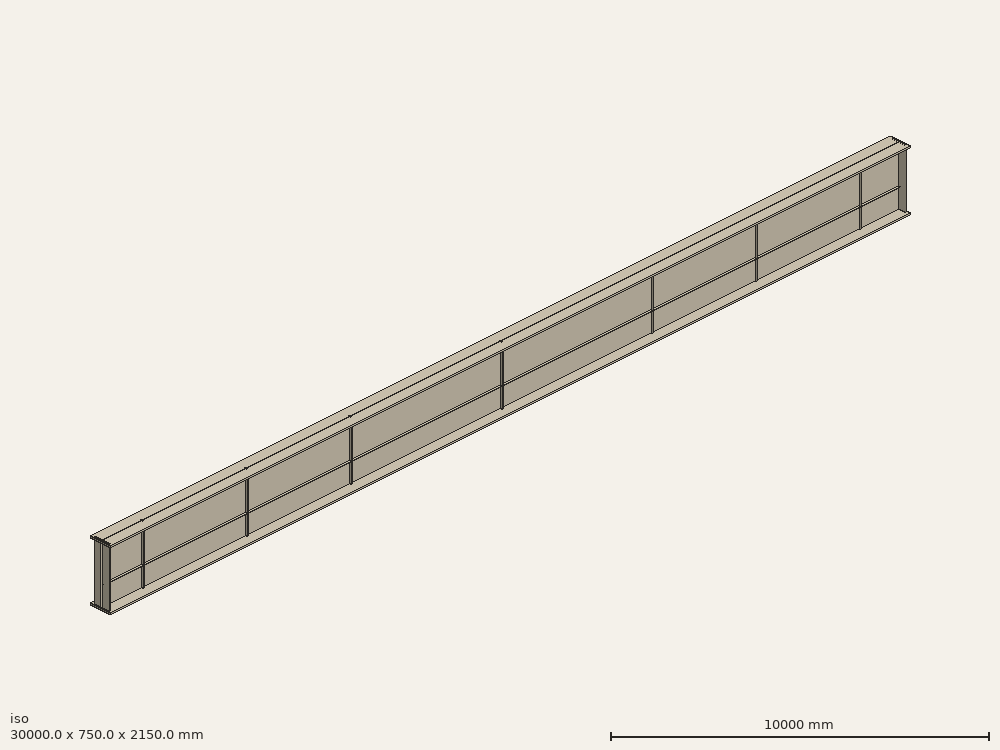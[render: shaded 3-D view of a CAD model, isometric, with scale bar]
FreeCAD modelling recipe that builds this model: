
FCSTD DOCUMENT  (FreeCAD 0.21R33771 (Git))
Label: Plate_girder_EC3_hvl
License: All rights reserved
LicenseURL: http://en.wikipedia.org/wiki/All_rights_reserved
objects: Sketcher::SketchObject×13, Part::Extrusion×13, Fem::ConstraintForce×5, Part::FeaturePython×2, Fem::ConstraintDisplacement×2, Fem::FemSolverObjectPython×1, App::MaterialObjectPython×1, Fem::FemMeshObjectPython×1, Fem::FemAnalysis×1, Part::Part2DObjectPython×1
note: 29 computed .brp shape members not serialized (recipe doc carries the construction recipe); baked Part::Feature solids carry a one-line shape summary decoded from their .brp

FEATURE [Fem::FemSolverObjectPython] SolverCcxTools  # FEM object (typed FeaturePython)
  AnalysisType = 0
  BeamShellResultOutput3D = false
  BucklingFactors = 1
  EigenmodeHighLimit = 1000000
  EigenmodeLowLimit = 0
  EigenmodesCount = 10
  GeometricalNonlinearity = 0
  IterationsControlParameterCutb = 0.25,0.5,0.75,0.85,,,1.5,
  IterationsControlParameterIter = 4,8,9,200,10,400,,200,,
  IterationsControlParameterTimeUse = false
  IterationsThermoMechMaximum = 2000
  IterationsUserDefinedIncrementations = false
  IterationsUserDefinedTimeStepLength = false
  MaterialNonlinearity = 0
  MatrixSolverType = 0
  SplitInputWriter = false
  ThermoMechSteadyState = true
  TimeEnd = 1
  TimeInitialStep = 0.01
FEATURE [App::MaterialObjectPython] MaterialSolid  # material (typed FeaturePython)
  Category = 0
  Material = AuthorAndLicense=(c) 2014 M. Münch - GNU Lesser General Public License (LGPL),CardName=Steel-St-E-315,Density=7800 kg/m^3,Father=Metal,+13 more (map truncated)
FEATURE [Sketcher::SketchObject] Sketch001  label="end stiffener"
  FullyConstrained = true
  Placement = pos=(0,0,0) rot=(0.57735,0.57735,0.57735;2.0944rad)
  sketch-geometry (4):
    g0: LineSegment StartX=87.5 StartY=2100 StartZ=0 EndX=662.5 EndY=2100 EndZ=0
    g1: LineSegment StartX=662.5 StartY=2100 StartZ=0 EndX=662.5 EndY=0 EndZ=0
    g2: LineSegment StartX=662.5 StartY=0 StartZ=0 EndX=87.5 EndY=0 EndZ=0
    g3: LineSegment StartX=87.5 StartY=0 StartZ=0 EndX=87.5 EndY=2100 EndZ=0
  constraints (12):
    c: Coincident(g0,g1)
    c: Coincident(g1,g2)
    c: Coincident(g2,g3)
    c: Coincident(g3,g0)
    c: Horizontal(g0)
    c: Horizontal(g2)
    c: Vertical(g1)
    c: Vertical(g3)
    c: DistanceY(g1,g1) = 2100
    c: PointOnObject(g2,g-1)
    c: DistanceX(g2,g2) = 575
    c: DistanceX(g-1,g2) = 87.5
FEATURE [Sketcher::SketchObject] Sketch002  label="stiffener"
  FullyConstrained = true
  Placement = pos=(0,0,0) rot=(0.57735,0.57735,0.57735;2.0944rad)
  sketch-geometry (4):
    g0: LineSegment StartX=287.5 StartY=2100 StartZ=0 EndX=462.5 EndY=2100 EndZ=0
    g1: LineSegment StartX=462.5 StartY=2100 StartZ=0 EndX=462.5 EndY=0 EndZ=0
    g2: LineSegment StartX=462.5 StartY=0 StartZ=0 EndX=287.5 EndY=0 EndZ=0
    g3: LineSegment StartX=287.5 StartY=0 StartZ=0 EndX=287.5 EndY=2100 EndZ=0
  constraints (12):
    c: Coincident(g0,g1)
    c: Coincident(g1,g2)
    c: Coincident(g2,g3)
    c: Coincident(g3,g0)
    c: Horizontal(g0)
    c: Horizontal(g2)
    c: Vertical(g1)
    c: Vertical(g3)
    c: DistanceY(g1,g1) = 2100
    c: PointOnObject(g2,g-1)
    c: DistanceX(g0,g0) = 175
    c: DistanceX(g-1,g2) = 287.5
FEATURE [Sketcher::SketchObject] Sketch003
  FullyConstrained = true
  sketch-geometry (4):
    g0: LineSegment StartX=0 StartY=462.5 StartZ=0 EndX=175 EndY=462.5 EndZ=0
    g1: LineSegment StartX=175 StartY=462.5 StartZ=0 EndX=175 EndY=287.5 EndZ=0
    g2: LineSegment StartX=175 StartY=287.5 StartZ=0 EndX=0 EndY=287.5 EndZ=0
    g3: LineSegment StartX=0 StartY=287.5 StartZ=0 EndX=0 EndY=462.5 EndZ=0
  constraints (12):
    c: Coincident(g0,g1)
    c: Coincident(g1,g2)
    c: Coincident(g2,g3)
    c: Coincident(g3,g0)
    c: Horizontal(g0)
    c: Horizontal(g2)
    c: Vertical(g1)
    c: Vertical(g3)
    c: DistanceX(g0,g0) = 175
    c: DistanceY(g1,g1) = 175
    c: PointOnObject(g2,g-2)
    c: DistanceY(g-1,g2) = 287.5
FEATURE [Part::Extrusion] Extrude001  label="load pad"
  Base = -> Sketch003
  Dir = (0,0,1)
  DirMode = 2
  FaceMakerClass = Part::FaceMakerBullseye
  LengthFwd = 0
  LengthRev = 50
  Placement = pos=(9262.5,0,0) rot=(0,0,1;0rad)
  Solid = true
  Symmetric = false
FEATURE [Part::Extrusion] Extrude002  label="stiffener001"
  Base = -> Sketch002
  Dir = (1,0,0)
  DirMode = 2
  FaceMakerClass = Part::FaceMakerBullseye
  LengthFwd = 15
  LengthRev = 0
  Placement = pos=(1542.5,0,0) rot=(0,0,1;0rad)
  Solid = true
  Symmetric = false
FEATURE [Part::Extrusion] Extrude003  label="end stiffener001"
  Base = -> Sketch001
  Dir = (1,0,0)
  DirMode = 2
  FaceMakerClass = Part::FaceMakerBullseye
  LengthFwd = 24
  LengthRev = 0
  Placement = pos=(50,0,0) rot=(0,0,1;0rad)
  Solid = true
  Symmetric = false
FEATURE [Sketcher::SketchObject] Sketch004  label="end stiffener003"
  FullyConstrained = true
  Placement = pos=(0,0,0) rot=(0.57735,0.57735,0.57735;2.0944rad)
  sketch-geometry (4):
    g0: LineSegment StartX=87.5 StartY=2100 StartZ=0 EndX=662.5 EndY=2100 EndZ=0
    g1: LineSegment StartX=662.5 StartY=2100 StartZ=0 EndX=662.5 EndY=0 EndZ=0
    g2: LineSegment StartX=662.5 StartY=0 StartZ=0 EndX=87.5 EndY=0 EndZ=0
    g3: LineSegment StartX=87.5 StartY=0 StartZ=0 EndX=87.5 EndY=2100 EndZ=0
  constraints (12):
    c: Coincident(g0,g1)
    c: Coincident(g1,g2)
    c: Coincident(g2,g3)
    c: Coincident(g3,g0)
    c: Horizontal(g0)
    c: Horizontal(g2)
    c: Vertical(g1)
    c: Vertical(g3)
    c: DistanceY(g1,g1) = 2100
    c: PointOnObject(g2,g-1)
    c: DistanceX(g2,g2) = 575
    c: DistanceX(g-1,g2) = 87.5
FEATURE [Part::Extrusion] Extrude004  label="end stiffener002"
  Base = -> Sketch004
  Dir = (1,0,0)
  DirMode = 2
  FaceMakerClass = Part::FaceMakerBullseye
  LengthFwd = 24
  LengthRev = 0
  Placement = pos=(29926,0,0) rot=(0,0,1;0rad)
  Solid = true
  Symmetric = false
FEATURE [Sketcher::SketchObject] Sketch005  label="stiffener003"
  FullyConstrained = true
  Placement = pos=(0,0,0) rot=(0.57735,0.57735,0.57735;2.0944rad)
  sketch-geometry (4):
    g0: LineSegment StartX=287.5 StartY=2100 StartZ=0 EndX=462.5 EndY=2100 EndZ=0
    g1: LineSegment StartX=462.5 StartY=2100 StartZ=0 EndX=462.5 EndY=0 EndZ=0
    g2: LineSegment StartX=462.5 StartY=0 StartZ=0 EndX=287.5 EndY=0 EndZ=0
    g3: LineSegment StartX=287.5 StartY=0 StartZ=0 EndX=287.5 EndY=2100 EndZ=0
  constraints (12):
    c: Coincident(g0,g1)
    c: Coincident(g1,g2)
    c: Coincident(g2,g3)
    c: Coincident(g3,g0)
    c: Horizontal(g0)
    c: Horizontal(g2)
    c: Vertical(g1)
    c: Vertical(g3)
    c: DistanceY(g1,g1) = 2100
    c: PointOnObject(g2,g-1)
    c: DistanceX(g0,g0) = 175
    c: DistanceX(g-1,g2) = 287.5
FEATURE [Part::Extrusion] Extrude005  label="stiffener002"
  Base = -> Sketch005
  Dir = (1,0,0)
  DirMode = 2
  FaceMakerClass = Part::FaceMakerBullseye
  LengthFwd = 15
  LengthRev = 0
  Placement = pos=(5442.5,0,0) rot=(0,0,1;0rad)
  Solid = true
  Symmetric = false
FEATURE [Sketcher::SketchObject] Sketch006  label="stiffener005"
  FullyConstrained = true
  Placement = pos=(0,0,0) rot=(0.57735,0.57735,0.57735;2.0944rad)
  sketch-geometry (4):
    g0: LineSegment StartX=287.5 StartY=2100 StartZ=0 EndX=462.5 EndY=2100 EndZ=0
    g1: LineSegment StartX=462.5 StartY=2100 StartZ=0 EndX=462.5 EndY=0 EndZ=0
    g2: LineSegment StartX=462.5 StartY=0 StartZ=0 EndX=287.5 EndY=0 EndZ=0
    g3: LineSegment StartX=287.5 StartY=0 StartZ=0 EndX=287.5 EndY=2100 EndZ=0
  constraints (12):
    c: Coincident(g0,g1)
    c: Coincident(g1,g2)
    c: Coincident(g2,g3)
    c: Coincident(g3,g0)
    c: Horizontal(g0)
    c: Horizontal(g2)
    c: Vertical(g1)
    c: Vertical(g3)
    c: DistanceY(g1,g1) = 2100
    c: PointOnObject(g2,g-1)
    c: DistanceX(g0,g0) = 175
    c: DistanceX(g-1,g2) = 287.5
FEATURE [Part::Extrusion] Extrude006  label="stiffener004"
  Base = -> Sketch006
  Dir = (1,0,0)
  DirMode = 2
  FaceMakerClass = Part::FaceMakerBullseye
  LengthFwd = 15
  LengthRev = 0
  Placement = pos=(9342.5,0,0) rot=(0,0,1;0rad)
  Solid = true
  Symmetric = false
FEATURE [Sketcher::SketchObject] Sketch007  label="stiffener007"
  FullyConstrained = true
  Placement = pos=(0,0,0) rot=(0.57735,0.57735,0.57735;2.0944rad)
  sketch-geometry (4):
    g0: LineSegment StartX=287.5 StartY=2100 StartZ=0 EndX=462.5 EndY=2100 EndZ=0
    g1: LineSegment StartX=462.5 StartY=2100 StartZ=0 EndX=462.5 EndY=0 EndZ=0
    g2: LineSegment StartX=462.5 StartY=0 StartZ=0 EndX=287.5 EndY=0 EndZ=0
    g3: LineSegment StartX=287.5 StartY=0 StartZ=0 EndX=287.5 EndY=2100 EndZ=0
  constraints (12):
    c: Coincident(g0,g1)
    c: Coincident(g1,g2)
    c: Coincident(g2,g3)
    c: Coincident(g3,g0)
    c: Horizontal(g0)
    c: Horizontal(g2)
    c: Vertical(g1)
    c: Vertical(g3)
    c: DistanceY(g1,g1) = 2100
    c: PointOnObject(g2,g-1)
    c: DistanceX(g0,g0) = 175
    c: DistanceX(g-1,g2) = 287.5
FEATURE [Part::Extrusion] Extrude007  label="stiffener006"
  Base = -> Sketch007
  Dir = (1,0,0)
  DirMode = 2
  FaceMakerClass = Part::FaceMakerBullseye
  LengthFwd = 15
  LengthRev = 0
  Placement = pos=(14992.5,0,0) rot=(0,0,1;0rad)
  Solid = true
  Symmetric = false
FEATURE [Sketcher::SketchObject] Sketch008  label="stiffener009"
  FullyConstrained = true
  Placement = pos=(0,0,0) rot=(0.57735,0.57735,0.57735;2.0944rad)
  sketch-geometry (4):
    g0: LineSegment StartX=287.5 StartY=2100 StartZ=0 EndX=462.5 EndY=2100 EndZ=0
    g1: LineSegment StartX=462.5 StartY=2100 StartZ=0 EndX=462.5 EndY=0 EndZ=0
    g2: LineSegment StartX=462.5 StartY=0 StartZ=0 EndX=287.5 EndY=0 EndZ=0
    g3: LineSegment StartX=287.5 StartY=0 StartZ=0 EndX=287.5 EndY=2100 EndZ=0
  constraints (12):
    c: Coincident(g0,g1)
    c: Coincident(g1,g2)
    c: Coincident(g2,g3)
    c: Coincident(g3,g0)
    c: Horizontal(g0)
    c: Horizontal(g2)
    c: Vertical(g1)
    c: Vertical(g3)
    c: DistanceY(g1,g1) = 2100
    c: PointOnObject(g2,g-1)
    c: DistanceX(g0,g0) = 175
    c: DistanceX(g-1,g2) = 287.5
FEATURE [Part::Extrusion] Extrude008  label="stiffener008"
  Base = -> Sketch008
  Dir = (1,0,0)
  DirMode = 2
  FaceMakerClass = Part::FaceMakerBullseye
  LengthFwd = 15
  LengthRev = 0
  Placement = pos=(20642.5,0,0) rot=(0,0,1;0rad)
  Solid = true
  Symmetric = false
FEATURE [Sketcher::SketchObject] Sketch009  label="stiffener011"
  FullyConstrained = true
  Placement = pos=(0,0,0) rot=(0.57735,0.57735,0.57735;2.0944rad)
  sketch-geometry (4):
    g0: LineSegment StartX=287.5 StartY=2100 StartZ=0 EndX=462.5 EndY=2100 EndZ=0
    g1: LineSegment StartX=462.5 StartY=2100 StartZ=0 EndX=462.5 EndY=0 EndZ=0
    g2: LineSegment StartX=462.5 StartY=0 StartZ=0 EndX=287.5 EndY=0 EndZ=0
    g3: LineSegment StartX=287.5 StartY=0 StartZ=0 EndX=287.5 EndY=2100 EndZ=0
  constraints (12):
    c: Coincident(g0,g1)
    c: Coincident(g1,g2)
    c: Coincident(g2,g3)
    c: Coincident(g3,g0)
    c: Horizontal(g0)
    c: Horizontal(g2)
    c: Vertical(g1)
    c: Vertical(g3)
    c: DistanceY(g1,g1) = 2100
    c: PointOnObject(g2,g-1)
    c: DistanceX(g0,g0) = 175
    c: DistanceX(g-1,g2) = 287.5
FEATURE [Part::Extrusion] Extrude009  label="stiffener010"
  Base = -> Sketch009
  Dir = (1,0,0)
  DirMode = 2
  FaceMakerClass = Part::FaceMakerBullseye
  LengthFwd = 15
  LengthRev = 0
  Placement = pos=(24542.5,0,0) rot=(0,0,1;0rad)
  Solid = true
  Symmetric = false
FEATURE [Sketcher::SketchObject] Sketch010  label="stiffener013"
  FullyConstrained = true
  Placement = pos=(0,0,0) rot=(0.57735,0.57735,0.57735;2.0944rad)
  sketch-geometry (4):
    g0: LineSegment StartX=287.5 StartY=2100 StartZ=0 EndX=462.5 EndY=2100 EndZ=0
    g1: LineSegment StartX=462.5 StartY=2100 StartZ=0 EndX=462.5 EndY=0 EndZ=0
    g2: LineSegment StartX=462.5 StartY=0 StartZ=0 EndX=287.5 EndY=0 EndZ=0
    g3: LineSegment StartX=287.5 StartY=0 StartZ=0 EndX=287.5 EndY=2100 EndZ=0
  constraints (12):
    c: Coincident(g0,g1)
    c: Coincident(g1,g2)
    c: Coincident(g2,g3)
    c: Coincident(g3,g0)
    c: Horizontal(g0)
    c: Horizontal(g2)
    c: Vertical(g1)
    c: Vertical(g3)
    c: DistanceY(g1,g1) = 2100
    c: PointOnObject(g2,g-1)
    c: DistanceX(g0,g0) = 175
    c: DistanceX(g-1,g2) = 287.5
FEATURE [Part::Extrusion] Extrude010  label="stiffener012"
  Base = -> Sketch010
  Dir = (1,0,0)
  DirMode = 2
  FaceMakerClass = Part::FaceMakerBullseye
  LengthFwd = 15
  LengthRev = 0
  Placement = pos=(28442.5,0,0) rot=(0,0,1;0rad)
  Solid = true
  Symmetric = false
FEATURE [Sketcher::SketchObject] Sketch  label="girder"
  FullyConstrained = true
  Placement = pos=(0,0,0) rot=(0.57735,0.57735,0.57735;2.0944rad)
  sketch-geometry (16):
    g0: LineSegment StartX=750 StartY=2100 StartZ=0 EndX=750 EndY=2050 EndZ=0
    g1: LineSegment StartX=750 StartY=2050 StartZ=0 EndX=382.5 EndY=2050 EndZ=0
    g2: LineSegment StartX=382.5 StartY=2050 StartZ=0 EndX=382.5 EndY=50 EndZ=0
    g3: LineSegment StartX=382.5 StartY=50 StartZ=0 EndX=750 EndY=50 EndZ=0
    g4: LineSegment StartX=750 StartY=50 StartZ=0 EndX=750 EndY=0 EndZ=0
    g5: LineSegment StartX=0 StartY=0 StartZ=0 EndX=0 EndY=50 EndZ=0
    g6: LineSegment StartX=0 StartY=50 StartZ=0 EndX=367.5 EndY=50 EndZ=0
    g7: LineSegment StartX=367.5 StartY=50 StartZ=0 EndX=367.5 EndY=2050 EndZ=0
    g8: LineSegment StartX=367.5 StartY=2050 StartZ=0 EndX=0 EndY=2050 EndZ=0
    g9: LineSegment StartX=750 StartY=2100 StartZ=0 EndX=382.5 EndY=2100 EndZ=0
    g10: LineSegment StartX=750 StartY=0 StartZ=0 EndX=382.5 EndY=0 EndZ=0
    g11: LineSegment StartX=367.5 StartY=0 StartZ=0 EndX=0 EndY=0 EndZ=0
    g12: LineSegment StartX=382.5 StartY=2100 StartZ=0 EndX=367.5 EndY=2100 EndZ=0
    g13: LineSegment StartX=0 StartY=2050 StartZ=0 EndX=0 EndY=2100 EndZ=0
    g14: LineSegment StartX=367.5 StartY=0 StartZ=0 EndX=382.5 EndY=0 EndZ=0
    g15: LineSegment StartX=0 StartY=2100 StartZ=0 EndX=367.5 EndY=2100 EndZ=0
  constraints (48):
    c: Vertical(g0)
    c: Coincident(g0,g1)
    c: Horizontal(g1)
    c: Coincident(g1,g2)
    c: Vertical(g2)
    c: Coincident(g2,g3)
    c: Horizontal(g3)
    c: Coincident(g3,g4)
    c: PointOnObject(g4,g-1)
    c: Vertical(g5)
    c: Coincident(g5,g6)
    c: Horizontal(g6)
    c: Coincident(g6,g7)
    c: Vertical(g7)
    c: Coincident(g7,g8)
    c: Horizontal(g8)
    c: Vertical(g4)
    c: DistanceY(g0,g0) = 50
    c: DistanceX(g6,g6) = 367.5
    c: DistanceX(g3,g3) = 367.5
    c: DistanceY(g4,g4) = 50
    c: DistanceY(g5,g5) = 50
    c: DistanceY(g4,g0) = 2100
    c: DistanceX(g-1,g5) = 0
    c: Coincident(g9,g0)
    c: Horizontal(g9)
    c: Coincident(g10,g4)
    c: Horizontal(g10)
    c: Coincident(g11,g5)
    c: Horizontal(g11)
    c: Coincident(g12,g9)
    c: Horizontal(g12)
    c: Coincident(g13,g8)
    c: Vertical(g13)
    c: DistanceX(g7,g1) = 15
    c: Equal(g11,g6)
    c: Equal(g10,g3)
    c: Coincident(g14,g11)
    c: Coincident(g14,g10)
    c: DistanceY(g13,g13) = 50
    c: DistanceY(g-1,g5) = 0
    c: Coincident(g15,g13)
    c: Coincident(g15,g12)
    c: Horizontal(g15)
    c: DistanceX(g15,g15) = 367.5
    c: DistanceX(g12,g12) = 15
    c: DistanceX(g9,g9) = 367.5
    c: PointOnObject(g13,g-2)
FEATURE [Part::Extrusion] Extrude
  Base = -> Sketch
  Dir = (1,0,0)
  DirMode = 2
  FaceMakerClass = Part::FaceMakerBullseye
  LengthFwd = 30000
  LengthRev = 0
  Solid = true
  Symmetric = false
FEATURE [Sketcher::SketchObject] Sketch011
  FullyConstrained = true
  sketch-geometry (4):
    g0: LineSegment StartX=0 StartY=462.5 StartZ=0 EndX=175 EndY=462.5 EndZ=0
    g1: LineSegment StartX=175 StartY=462.5 StartZ=0 EndX=175 EndY=287.5 EndZ=0
    g2: LineSegment StartX=175 StartY=287.5 StartZ=0 EndX=0 EndY=287.5 EndZ=0
    g3: LineSegment StartX=0 StartY=287.5 StartZ=0 EndX=0 EndY=462.5 EndZ=0
  constraints (12):
    c: Coincident(g0,g1)
    c: Coincident(g1,g2)
    c: Coincident(g2,g3)
    c: Coincident(g3,g0)
    c: Horizontal(g0)
    c: Horizontal(g2)
    c: Vertical(g1)
    c: Vertical(g3)
    c: DistanceX(g0,g0) = 175
    c: DistanceY(g1,g1) = 175
    c: PointOnObject(g2,g-2)
    c: DistanceY(g-1,g2) = 287.5
FEATURE [Part::Extrusion] Extrude011  label="load pad001"
  Base = -> Sketch011
  Dir = (0,0,1)
  DirMode = 2
  FaceMakerClass = Part::FaceMakerBullseye
  LengthFwd = 0
  LengthRev = 50
  Placement = pos=(20562.5,0,0) rot=(0,0,1;0rad)
  Solid = true
  Symmetric = false
FEATURE [Part::FeaturePython] BooleanFragments  # WARN: FeaturePython — macro-defined, semantics opaque (R4)
  Mode = 2
  Objects = -> [Extrude001,Extrude002,Extrude003,Extrude004,Extrude005,Extrude006,Extrude007,Extrude008,Extrude009,Extrude010,Extrude,Extrude011]
  Tolerance = 0
FEATURE [Fem::ConstraintDisplacement] ConstraintDisplacement003
  NormalDirection = (0,0,1)
  Normals = (10) [(0,0,1),(0,0,1),(0,0,1),(0,0,1),(0,0,1),(0,0,1),(0,0,1),(0,0,1),(0,0,1),(0,0,1)]
  Points = (10) [(50,87.5,2100),(50,180.833,2100),(50,274.167,2100),(50,367.5,2100),(50,367.5,2100),(50,382.5,2100),(50,382.5,2100),(50,475.833,2100),+2 more]
  References = -> [BooleanFragments]
  Scale = 18
  hasXFormula = false
  hasYFormula = false
  hasZFormula = false
  rotxFix = false
  rotxFree = true
  rotyFix = false
  rotyFree = true
  rotzFix = false
  rotzFree = true
  useFlowSurfaceForce = false
  xDisplacement = 0
  xFix = false
  xFree = false
  xRotation = 0
  yDisplacement = 0
  yFix = false
  yFree = false
  yRotation = 0
  zDisplacement = 0
  zFix = false
  zFree = false
  zRotation = 0
FEATURE [Fem::ConstraintDisplacement] ConstraintDisplacement004
  NormalDirection = (0,0,1)
  Normals = (10) [(0,0,1),(0,0,1),(0,0,1),(0,0,1),(0,0,1),(0,0,1),(0,0,1),(0,0,1),(0,0,1),(0,0,1)]
  Points = (10) [(29950,87.5,2100),(29950,180.833,2100),(29950,274.167,2100),(29950,367.5,2100),(29950,367.5,2100),(29950,382.5,2100),(29950,382.5,2100),+3 more]
  References = -> [BooleanFragments]
  Scale = 18
  hasXFormula = false
  hasYFormula = false
  hasZFormula = false
  rotxFix = false
  rotxFree = true
  rotyFix = false
  rotyFree = true
  rotzFix = false
  rotzFree = true
  useFlowSurfaceForce = false
  xDisplacement = 0
  xFix = false
  xFree = true
  xRotation = 0
  yDisplacement = 0
  yFix = false
  yFree = false
  yRotation = 0
  zDisplacement = 0
  zFix = false
  zFree = false
  zRotation = 0
FEATURE [Fem::ConstraintForce] ConstraintForce005
  DirectionVector = (0,0,-1)
  Force = 2293000
  NormalDirection = (0,0,1)
  Points = (33) [(29950,87.5,2100),(29950,180.833,2100),(29950,274.167,2100),(29950,367.5,2100),(29938,87.5,2100),(29938,180.833,2100),(29938,274.167,2100),+26 more]
  References = -> [BooleanFragments]
  Reversed = true
  Scale = 13
FEATURE [Fem::ConstraintForce] ConstraintForce006
  DirectionVector = (0,0,-1)
  Force = 2293000
  NormalDirection = (0,0,1)
  Points = (33) [(74,87.5,2100),(74,180.833,2100),(74,274.167,2100),(74,367.5,2100),(62,87.5,2100),(62,180.833,2100),(62,274.167,2100),(62,367.5,2100),(50,87.5,2100),+24 more]
  References = -> [BooleanFragments]
  Reversed = true
  Scale = 13
FEATURE [Fem::ConstraintForce] ConstraintForce007
  DirectionVector = (0,0,1)
  Force = 925000
  NormalDirection = (0,0,-1)
  Points = (16) [(9262.5,287.5,-50),(9320.83,287.5,-50),(9379.17,287.5,-50),(9437.5,287.5,-50),(9262.5,345.833,-50),(9320.83,345.833,-50),(9379.17,345.833,-50),+9 more]
  References = -> [BooleanFragments]
  Reversed = true
  Scale = 14
FEATURE [Fem::ConstraintForce] ConstraintForce008
  DirectionVector = (0,0,1)
  Force = 925000
  NormalDirection = (0,0,-1)
  Points = (16) [(20562.5,287.5,-50),(20620.8,287.5,-50),(20679.2,287.5,-50),(20737.5,287.5,-50),(20562.5,345.833,-50),(20620.8,345.833,-50),(20679.2,345.833,-50),+9 more]
  References = -> [BooleanFragments]
  Reversed = true
  Scale = 14
FEATURE [Sketcher::SketchObject] Sketch012
  FullyConstrained = true
  Placement = pos=(0,0,0) rot=(0.57735,0.57735,0.57735;2.0944rad)
  sketch-geometry (4):
    g0: LineSegment StartX=287.5 StartY=765 StartZ=0 EndX=462.5 EndY=765 EndZ=0
    g1: LineSegment StartX=462.5 StartY=765 StartZ=0 EndX=462.5 EndY=750 EndZ=0
    g2: LineSegment StartX=462.5 StartY=750 StartZ=0 EndX=287.5 EndY=750 EndZ=0
    g3: LineSegment StartX=287.5 StartY=750 StartZ=0 EndX=287.5 EndY=765 EndZ=0
  constraints (12):
    c: Coincident(g0,g1)
    c: Coincident(g1,g2)
    c: Coincident(g2,g3)
    c: Coincident(g3,g0)
    c: Horizontal(g0)
    c: Horizontal(g2)
    c: Vertical(g1)
    c: Vertical(g3)
    c: DistanceX(g2,g2) = 175
    c: DistanceY(g1,g1) = 15
    c: DistanceY(g-1,g2) = 750
    c: DistanceX(g-1,g2) = 287.5
FEATURE [Part::Extrusion] Extrude012
  Base = -> Sketch012
  Dir = (1,0,0)
  DirMode = 2
  FaceMakerClass = Part::FaceMakerBullseye
  LengthFwd = 29900
  LengthRev = 0
  Placement = pos=(50,0,0) rot=(0,0,1;0rad)
  Solid = true
  Symmetric = false
FEATURE [Part::FeaturePython] BooleanFragments001  # WARN: FeaturePython — macro-defined, semantics opaque (R4)
  Mode = 2
  Objects = -> [BooleanFragments,Extrude012]
  Tolerance = 0
FEATURE [Fem::ConstraintForce] ConstraintForce009
  DirectionVector = (0,0,1)
  Force = 2736000
  NormalDirection = (0,0,-1)
  Points = (315) [(50,367.5,0),(50,375,0),(50,382.5,0),(33.3333,367.5,0),(33.3333,375,0),(33.3333,382.5,0),(16.6667,367.5,0),(16.6667,375,0),(16.6667,382.5,0),+306 more]
  References = -> [BooleanFragments001]
  Reversed = true
FEATURE [Fem::FemMeshObjectPython] FEMMeshGmsh  # FEM object (typed FeaturePython)
  Algorithm2D = 0
  Algorithm3D = 0
  CharacteristicLengthMax = 290
  CharacteristicLengthMin = 0
  CoherenceMesh = true
  ElementDimension = 3
  ElementOrder = 1
  GeometryTolerance = 1e-06
  GroupsOfNodes = false
  HighOrderOptimize = 0
  MeshSizeFromCurvature = 12
  OptimizeNetgen = false
  OptimizeStd = true
  Part = -> BooleanFragments001
  RecombinationAlgorithm = 0
  Recombine3DAll = false
  RecombineAll = false
  SecondOrderLinear = false
FEATURE [Fem::FemAnalysis] Analysis
  Group = -> [SolverCcxTools,MaterialSolid,ConstraintDisplacement003,ConstraintDisplacement004,ConstraintForce005,ConstraintForce006,ConstraintForce007,ConstraintForce008,ConstraintForce009,FEMMeshGmsh]
FEATURE [Part::Part2DObjectPython] Line  # Draft 2D object (typed FeaturePython)
  Area = 0
  ChamferSize = 0
  Closed = false
  End = (-391.75,462.5,50)
  FilletRadius = 0
  Length = 700
  MakeFace = true
  Placement = pos=(-391.75,462.5,750) rot=(-0.739328,0.624306,-0.252263;1.185rad)
  Points = (2) [(0,0,0),(323.466,548.248,-291.194)]
  Start = (-391.75,462.5,750)
  Subdivisions = 0
